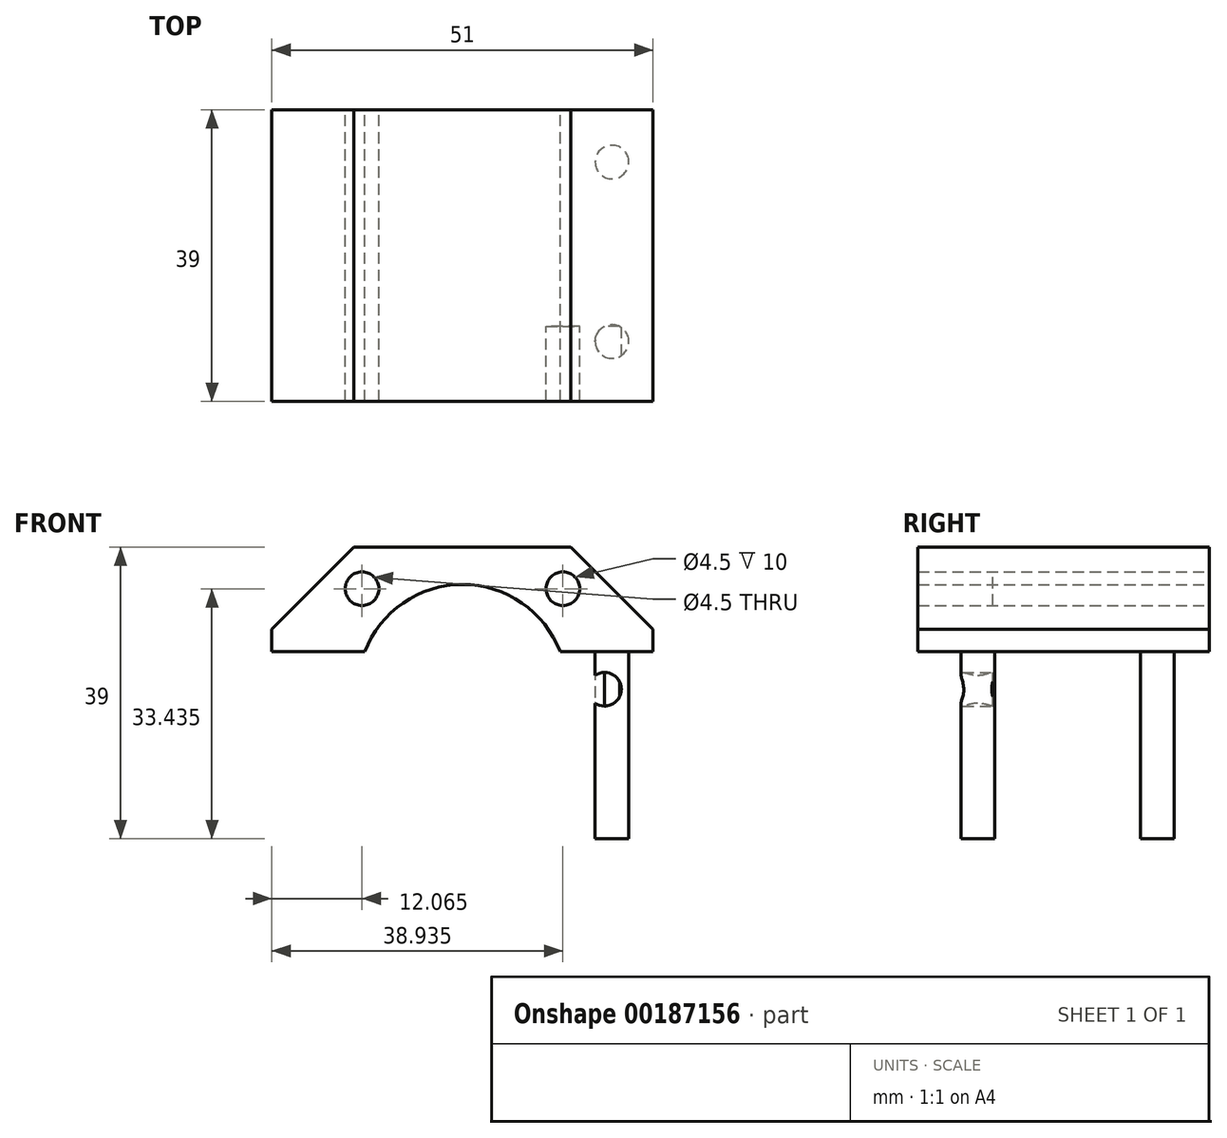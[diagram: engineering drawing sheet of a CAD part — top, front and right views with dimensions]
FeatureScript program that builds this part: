
annotation { "Feature Type Name" : "Feature", "Feature Type Description" : "" }
export const myFeature = defineFeature(function(context is Context, id is Id, definition is map)
    precondition{}
    {
        {
            var Q0;
            Q0=qCreatedBy(makeId("Front.planeOp"),FACE);
            var sketch = newSketch(context, id + "F0", { "sketchPlane" : qUnion([Q0])});
            skLineSegment(sketch, "E0.bottom", {"start": v(25.5, -14) * mm, "end": v(-25.5, -14) * mm});
            skLineSegment(sketch, "E0.left", {"start": v(25.5, -14) * mm, "end": v(25.5, 14) * mm});
            skLineSegment(sketch, "E0.right", {"start": v(-25.5, -14) * mm, "end": v(-25.5, 14) * mm});
            skPoint(sketch, "E0.middle", {"position": v(0, 0) * mm});
            skLineSegment(sketch, "E1", {"start": v(-25.5, 14) * mm, "end": v(-14.5, 25) * mm});
            skLineSegment(sketch, "E2", {"start": v(-14.5, 25) * mm, "end": v(14.5, 25) * mm});
            skLineSegment(sketch, "E3", {"start": v(14.5, 25) * mm, "end": v(25.5, 14) * mm});
            skCircle(sketch, "E4", {"center": v(0, 6) * mm, "radius": 14 * mm});
            skCircle(sketch, "E5", {"center": v(0, 6) * mm, "radius": 19 * mm, "construction": true});
            skLineSegment(sketch, "E6", {"start": v(0, 6) * mm, "end": v(19, 6) * mm, "construction": true});
            skLineSegment(sketch, "E7", {"start": v(0, 6) * mm, "end": v(13.44, 19.44) * mm, "construction": true});
            skCircle(sketch, "E8", {"center": v(13.44, 19.44) * mm, "radius": 2.25 * mm});
            skCircle(sketch, "E9", {"center": v(19, 6) * mm, "radius": 2.25 * mm});
            skCircle(sketch, "E10.MirrorC", {"center": v(13.44, -7.44) * mm, "radius": 2.25 * mm});
            skLineSegment(sketch, "E11", {"start": v(0, 25) * mm, "end": v(0, -14) * mm, "construction": true});
            skCircle(sketch, "E12.MirrorC", {"center": v(-13.44, -7.44) * mm, "radius": 2.25 * mm});
            skCircle(sketch, "E13.MirrorC", {"center": v(-19, 6) * mm, "radius": 2.25 * mm});
            skCircle(sketch, "E14.MirrorC", {"center": v(-13.44, 19.44) * mm, "radius": 2.25 * mm});
            skSolve(sketch);
        }
        {
            var Q0;
            Q0=makeQuery(id+"F0.imprint","IMPRINT",FACE,{"disambiguationData":[TD([[makeQuery(id+"F0.imprint","IMPRINT",EDGE,{"derivedFrom":sQuery(id+"F0.wireOp",EDGE,"E0.bottom")}),-1.0]])]});
            extrude(context, id + "F2", {"entities" : qUnion([Q0]), "depth" : 39 * mm});
        }
        {
            var Q0;
            Q0=makeQuery(id+"F0.imprint","IMPRINT",FACE,{"disambiguationData":[TD([[makeQuery(id+"F0.imprint","IMPRINT",EDGE,{"derivedFrom":sQuery(id+"F0.wireOp",EDGE,"E9")}),1.0]])]});
            var Q1;
            Q1=makeQuery(id+"F0.imprint","IMPRINT",FACE,{"disambiguationData":[TD([[makeQuery(id+"F0.imprint","IMPRINT",EDGE,{"derivedFrom":sQuery(id+"F0.wireOp",EDGE,"E8")}),1.0]])]});
            var Q2;
            Q2=makeQuery(id+"F0.imprint","IMPRINT",FACE,{"disambiguationData":[TD([[makeQuery(id+"F0.imprint","IMPRINT",EDGE,{"derivedFrom":sQuery(id+"F0.wireOp",EDGE,"E10.MirrorC")}),-1.0]])]});
            var Q3;
            Q3=makeQuery(id+"F0.imprint","IMPRINT",FACE,{"disambiguationData":[TD([[makeQuery(id+"F0.imprint","IMPRINT",EDGE,{"derivedFrom":sQuery(id+"F0.wireOp",EDGE,"E12.MirrorC")}),1.0]])]});
            var Q4;
            Q4=makeQuery(id+"F0.imprint","IMPRINT",FACE,{"disambiguationData":[TD([[makeQuery(id+"F0.imprint","IMPRINT",EDGE,{"derivedFrom":sQuery(id+"F0.wireOp",EDGE,"E13.MirrorC")}),-1.0]])]});
            var Q5;
            Q5=makeQuery(id+"F0.imprint","IMPRINT",FACE,{"disambiguationData":[TD([[makeQuery(id+"F0.imprint","IMPRINT",EDGE,{"derivedFrom":sQuery(id+"F0.wireOp",EDGE,"E14.MirrorC")}),-1.0]])]});
            extrude(context, id + "F3", {"entities" : qUnion([Q0, Q1, Q2, Q3, Q4, Q5]), "operationType" : NewBodyOperationType.ADD, "depth" : 29 * mm});
        }
        {
            var Q0;
            Q0=makeQuery(id+"F2.opExtrude","SWEPT_FACE",FACE,{"disambiguationData":[OSD([sQuery(id+"F0.wireOp",EDGE,"E0.bottom")])]});
            var sketch = newSketch(context, id + "F1", { "sketchPlane" : qUnion([Q0])});
            skCircle(sketch, "E15", {"center": v(-20, 31) * mm, "radius": 2.25 * mm});
            skCircle(sketch, "E16", {"center": v(-20, 7) * mm, "radius": 2.25 * mm});
            skLineSegment(sketch, "E17", {"start": v(0, 43.64) * mm, "end": v(0, 0) * mm, "construction": true});
            skCircle(sketch, "E18.MirrorC", {"center": v(20, 31) * mm, "radius": 2.25 * mm});
            skCircle(sketch, "E19.MirrorC", {"center": v(20, 7) * mm, "radius": 2.25 * mm});
            skSolve(sketch);
        }
        {
            var Q0;
            Q0=makeQuery(id+"F1.imprint","IMPRINT",FACE,{"disambiguationData":[TD([[makeQuery(id+"F1.imprint","IMPRINT",EDGE,{"derivedFrom":sQuery(id+"F1.wireOp",EDGE,"E16")}),1.0]])]});
            var Q1;
            Q1=makeQuery(id+"F1.imprint","IMPRINT",FACE,{"disambiguationData":[TD([[makeQuery(id+"F1.imprint","IMPRINT",EDGE,{"derivedFrom":sQuery(id+"F1.wireOp",EDGE,"E15")}),1.0]])]});
            var Q2;
            Q2=makeQuery(id+"F1.imprint","IMPRINT",FACE,{"disambiguationData":[TD([[makeQuery(id+"F1.imprint","IMPRINT",EDGE,{"derivedFrom":sQuery(id+"F1.wireOp",EDGE,"E18.MirrorC")}),-1.0]])]});
            var Q3;
            Q3=makeQuery(id+"F1.imprint","IMPRINT",FACE,{"disambiguationData":[TD([[makeQuery(id+"F1.imprint","IMPRINT",EDGE,{"derivedFrom":sQuery(id+"F1.wireOp",EDGE,"E19.MirrorC")}),-1.0]])]});
            extrude(context, id + "F4", {"entities" : qUnion([Q0, Q1, Q2, Q3]), "operationType" : NewBodyOperationType.REMOVE, "oppositeDirection" : true, "depth" : 25 * mm});
        }
    });
